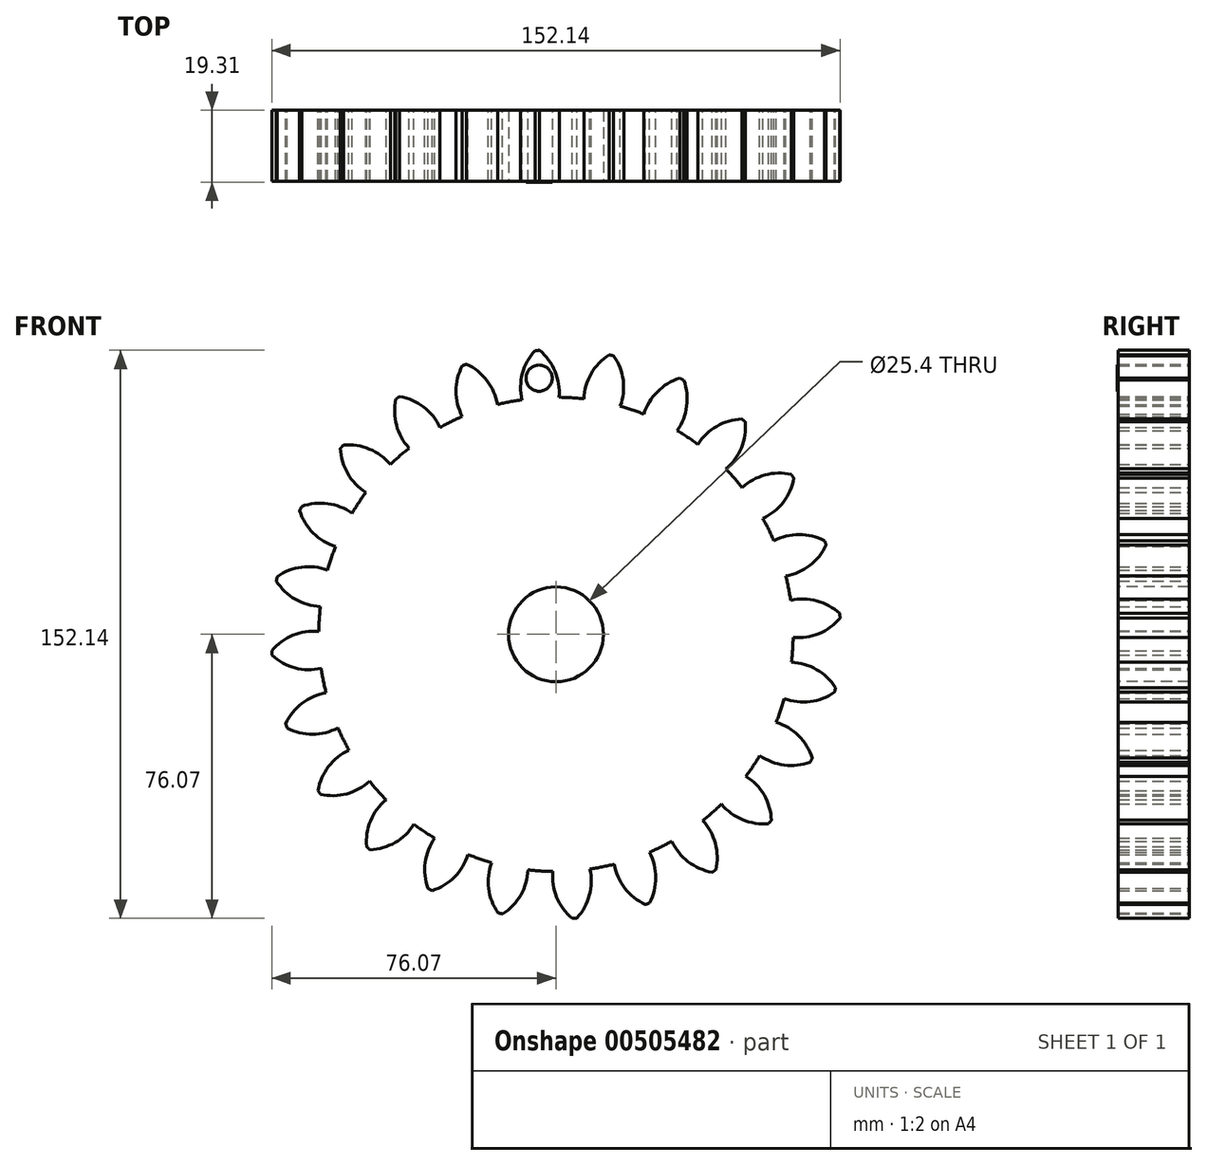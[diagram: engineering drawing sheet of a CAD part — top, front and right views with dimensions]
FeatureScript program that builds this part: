
annotation { "Feature Type Name" : "Feature", "Feature Type Description" : "" }
export const myFeature = defineFeature(function(context is Context, id is Id, definition is map)
    precondition{}
    {
        {
            var Q0;
            Q0=qCreatedBy(makeId("Front.planeOp"),FACE);
            var sketch = newSketch(context, id + "F0", { "sketchPlane" : qUnion([Q0])});
            skPoint(sketch, "E0.rect.middle", {"position": v(0, 0) * mm});
            skLineSegment(sketch, "E1", {"start": v(0, 0) * mm, "end": v(0, 76.2) * mm});
            skLineSegment(sketch, "E2", {"start": v(0, 0) * mm, "end": v(0, -76.2) * mm});
            skLineSegment(sketch, "E3", {"start": v(0, 0) * mm, "end": v(19.72, 73.6) * mm});
            skLineSegment(sketch, "E4", {"start": v(0, 0) * mm, "end": v(38.1, 66) * mm});
            skLineSegment(sketch, "E5", {"start": v(0, 0) * mm, "end": v(53.88, 53.88) * mm});
            skLineSegment(sketch, "E6", {"start": v(0, 0) * mm, "end": v(66, 38.1) * mm});
            skLineSegment(sketch, "E7", {"start": v(0, 0) * mm, "end": v(73.6, 19.72) * mm});
            skLineSegment(sketch, "E8", {"start": v(0, 0) * mm, "end": v(76.2, 0) * mm});
            skLineSegment(sketch, "E9", {"start": v(0, 0) * mm, "end": v(73.6, -19.72) * mm});
            skLineSegment(sketch, "E10", {"start": v(0, 0) * mm, "end": v(66, -38.1) * mm});
            skLineSegment(sketch, "E11", {"start": v(0, 0) * mm, "end": v(53.88, -53.88) * mm});
            skLineSegment(sketch, "E12", {"start": v(0, 0) * mm, "end": v(38.1, -66) * mm});
            skLineSegment(sketch, "E13", {"start": v(0, 0) * mm, "end": v(19.72, -73.6) * mm});
            skLineSegment(sketch, "E14", {"start": v(0, 0) * mm, "end": v(-19.72, -73.6) * mm});
            skLineSegment(sketch, "E15", {"start": v(0, 0) * mm, "end": v(-38.1, -66) * mm});
            skLineSegment(sketch, "E16", {"start": v(0, 0) * mm, "end": v(-53.88, -53.88) * mm});
            skLineSegment(sketch, "E17", {"start": v(0, 0) * mm, "end": v(-66, -38.1) * mm});
            skLineSegment(sketch, "E18", {"start": v(0, 0) * mm, "end": v(-73.6, -19.72) * mm});
            skLineSegment(sketch, "E19", {"start": v(0, 0) * mm, "end": v(-76.2, 0.07) * mm});
            skLineSegment(sketch, "E20", {"start": v(0, 0) * mm, "end": v(-73.6, 19.72) * mm});
            skLineSegment(sketch, "E21", {"start": v(0, 0) * mm, "end": v(-66, 38.1) * mm});
            skLineSegment(sketch, "E22", {"start": v(0, 0) * mm, "end": v(-53.88, 53.88) * mm});
            skLineSegment(sketch, "E23", {"start": v(0, 0) * mm, "end": v(-38.1, 66) * mm});
            skLineSegment(sketch, "E24", {"start": v(0, 0) * mm, "end": v(-19.72, 73.6) * mm});
            skCircle(sketch, "E25", {"center": v(0, 0) * mm, "radius": 76.2 * mm});
            skCircle(sketch, "E26", {"center": v(0, 0) * mm, "radius": 69.85 * mm});
            skCircle(sketch, "E27", {"center": v(0, 0) * mm, "radius": 63.5 * mm});
            skLineSegment(sketch, "E28", {"start": v(0, 0) * mm, "end": v(-4.98, 76.04) * mm});
            skLineSegment(sketch, "E29", {"start": v(0, 69.85) * mm, "end": v(-76.58, 69.85) * mm});
            skLineSegment(sketch, "E30", {"start": v(0, 69.85) * mm, "end": v(-76.5, 42) * mm});
            skLineSegment(sketch, "E31", {"start": v(-4.98, 76.04) * mm, "end": v(-7.15, 109.16) * mm});
            skLineSegment(sketch, "E32", {"start": v(0, 76.2) * mm, "end": v(0, 110.22) * mm});
            skCircle(sketch, "E33", {"center": v(0, 69.85) * mm, "radius": 14.6 * mm});
            skPoint(sketch, "E34", {"position": v(-13.72, 64.85) * mm});
            skArc(sketch, "E35", {"start": v(0.82, 63.5) * mm, "mid": v(-0.22, 70.43) * mm, "end": v(-4.37, 76.07) * mm});
            skArc(sketch, "E36.MirrorCS", {"start": v(-9.1, 62.84) * mm, "mid": v(-8.97, 69.85) * mm, "end": v(-5.6, 76) * mm});
            skSolve(sketch);
        }
        {
            var Q0;
            {var subQ1=sQuery(id+"F0.wireOp",EDGE,"E23");var subQ3=sQuery(id+"F0.wireOp",EDGE,"E27");var subQ4=makeQuery(id+"F0.imprint","INTERSECT",VERTEX,{"derivedFrom":[subQ1,subQ3]});Q0=makeQuery(id+"F0.imprint","IMPRINT",FACE,{"disambiguationData":[TD([[makeQuery(id+"F0.imprint","IMPRINT",EDGE,{"disambiguationData":[TD([[subQ4,1.0]])],"derivedFrom":subQ3}),1.0]])]});}
            var Q1;
            {var subQ1=sQuery(id+"F0.wireOp",EDGE,"E22");var subQ3=sQuery(id+"F0.wireOp",EDGE,"E27");var subQ4=makeQuery(id+"F0.imprint","INTERSECT",VERTEX,{"derivedFrom":[subQ1,subQ3]});Q1=makeQuery(id+"F0.imprint","IMPRINT",FACE,{"disambiguationData":[TD([[makeQuery(id+"F0.imprint","IMPRINT",EDGE,{"disambiguationData":[TD([[subQ4,1.0]])],"derivedFrom":subQ3}),1.0]])]});}
            var Q2;
            {var subQ1=sQuery(id+"F0.wireOp",EDGE,"E1");var subQ3=sQuery(id+"F0.wireOp",EDGE,"E33");var subQ4=makeQuery(id+"F0.imprint","INTERSECT",VERTEX,{"derivedFrom":[subQ1,subQ3]});Q2=makeQuery(id+"F0.imprint","IMPRINT",FACE,{"disambiguationData":[TD([[makeQuery(id+"F0.imprint","IMPRINT",EDGE,{"disambiguationData":[TD([[subQ4,1.0]])],"derivedFrom":subQ3}),-1.0]])]});}
            var Q3;
            {var subQ1=sQuery(id+"F0.wireOp",EDGE,"E19");var subQ3=sQuery(id+"F0.wireOp",EDGE,"E27");var subQ4=makeQuery(id+"F0.imprint","INTERSECT",VERTEX,{"derivedFrom":[subQ1,subQ3]});Q3=makeQuery(id+"F0.imprint","IMPRINT",FACE,{"disambiguationData":[TD([[makeQuery(id+"F0.imprint","IMPRINT",EDGE,{"disambiguationData":[TD([[subQ4,1.0]])],"derivedFrom":subQ3}),1.0]])]});}
            var Q4;
            {var subQ1=sQuery(id+"F0.wireOp",EDGE,"E24");var subQ3=sQuery(id+"F0.wireOp",EDGE,"E27");var subQ4=makeQuery(id+"F0.imprint","INTERSECT",VERTEX,{"derivedFrom":[subQ1,subQ3]});Q4=makeQuery(id+"F0.imprint","IMPRINT",FACE,{"disambiguationData":[TD([[makeQuery(id+"F0.imprint","IMPRINT",EDGE,{"disambiguationData":[TD([[subQ4,1.0]])],"derivedFrom":subQ3}),1.0]])]});}
            var Q5;
            {var subQ1=sQuery(id+"F0.wireOp",EDGE,"E20");var subQ3=sQuery(id+"F0.wireOp",EDGE,"E27");var subQ4=makeQuery(id+"F0.imprint","INTERSECT",VERTEX,{"derivedFrom":[subQ1,subQ3]});Q5=makeQuery(id+"F0.imprint","IMPRINT",FACE,{"disambiguationData":[TD([[makeQuery(id+"F0.imprint","IMPRINT",EDGE,{"disambiguationData":[TD([[subQ4,1.0]])],"derivedFrom":subQ3}),1.0]])]});}
            var Q6;
            {var subQ1=sQuery(id+"F0.wireOp",EDGE,"E21");var subQ3=sQuery(id+"F0.wireOp",EDGE,"E27");var subQ4=makeQuery(id+"F0.imprint","INTERSECT",VERTEX,{"derivedFrom":[subQ1,subQ3]});Q6=makeQuery(id+"F0.imprint","IMPRINT",FACE,{"disambiguationData":[TD([[makeQuery(id+"F0.imprint","IMPRINT",EDGE,{"disambiguationData":[TD([[subQ4,1.0]])],"derivedFrom":subQ3}),1.0]])]});}
            var Q7;
            {var subQ1=sQuery(id+"F0.wireOp",EDGE,"E6");var subQ3=sQuery(id+"F0.wireOp",EDGE,"E27");var subQ4=makeQuery(id+"F0.imprint","INTERSECT",VERTEX,{"derivedFrom":[subQ1,subQ3]});Q7=makeQuery(id+"F0.imprint","IMPRINT",FACE,{"disambiguationData":[TD([[makeQuery(id+"F0.imprint","IMPRINT",EDGE,{"disambiguationData":[TD([[subQ4,1.0]])],"derivedFrom":subQ3}),1.0]])]});}
            var Q8;
            {var subQ1=sQuery(id+"F0.wireOp",EDGE,"E4");var subQ3=sQuery(id+"F0.wireOp",EDGE,"E27");var subQ4=makeQuery(id+"F0.imprint","INTERSECT",VERTEX,{"derivedFrom":[subQ1,subQ3]});Q8=makeQuery(id+"F0.imprint","IMPRINT",FACE,{"disambiguationData":[TD([[makeQuery(id+"F0.imprint","IMPRINT",EDGE,{"disambiguationData":[TD([[subQ4,1.0]])],"derivedFrom":subQ3}),1.0]])]});}
            var Q9;
            {var subQ1=sQuery(id+"F0.wireOp",EDGE,"E7");var subQ3=sQuery(id+"F0.wireOp",EDGE,"E27");var subQ4=makeQuery(id+"F0.imprint","INTERSECT",VERTEX,{"derivedFrom":[subQ1,subQ3]});Q9=makeQuery(id+"F0.imprint","IMPRINT",FACE,{"disambiguationData":[TD([[makeQuery(id+"F0.imprint","IMPRINT",EDGE,{"disambiguationData":[TD([[subQ4,1.0]])],"derivedFrom":subQ3}),1.0]])]});}
            var Q10;
            {var subQ0=sQuery(id+"F0.wireOp",EDGE,"E3");var subQ5=sQuery(id+"F0.wireOp",EDGE,"E27");var subQ6=makeQuery(id+"F0.imprint","INTERSECT",VERTEX,{"derivedFrom":[subQ0,subQ5]});Q10=makeQuery(id+"F0.imprint","IMPRINT",FACE,{"disambiguationData":[TD([[makeQuery(id+"F0.imprint","IMPRINT",EDGE,{"disambiguationData":[TD([[subQ6,-1.0]])],"derivedFrom":subQ5}),1.0]])]});}
            var Q11;
            {var subQ1=sQuery(id+"F0.wireOp",EDGE,"E3");var subQ3=sQuery(id+"F0.wireOp",EDGE,"E27");var subQ4=makeQuery(id+"F0.imprint","INTERSECT",VERTEX,{"derivedFrom":[subQ1,subQ3]});Q11=makeQuery(id+"F0.imprint","IMPRINT",FACE,{"disambiguationData":[TD([[makeQuery(id+"F0.imprint","IMPRINT",EDGE,{"disambiguationData":[TD([[subQ4,1.0]])],"derivedFrom":subQ3}),1.0]])]});}
            var Q12;
            {var subQ1=sQuery(id+"F0.wireOp",EDGE,"E5");var subQ3=sQuery(id+"F0.wireOp",EDGE,"E27");var subQ4=makeQuery(id+"F0.imprint","INTERSECT",VERTEX,{"derivedFrom":[subQ1,subQ3]});Q12=makeQuery(id+"F0.imprint","IMPRINT",FACE,{"disambiguationData":[TD([[makeQuery(id+"F0.imprint","IMPRINT",EDGE,{"disambiguationData":[TD([[subQ4,1.0]])],"derivedFrom":subQ3}),1.0]])]});}
            var Q13;
            {var subQ1=sQuery(id+"F0.wireOp",EDGE,"E17");var subQ3=sQuery(id+"F0.wireOp",EDGE,"E27");var subQ4=makeQuery(id+"F0.imprint","INTERSECT",VERTEX,{"derivedFrom":[subQ1,subQ3]});Q13=makeQuery(id+"F0.imprint","IMPRINT",FACE,{"disambiguationData":[TD([[makeQuery(id+"F0.imprint","IMPRINT",EDGE,{"disambiguationData":[TD([[subQ4,1.0]])],"derivedFrom":subQ3}),1.0]])]});}
            var Q14;
            {var subQ1=sQuery(id+"F0.wireOp",EDGE,"E15");var subQ3=sQuery(id+"F0.wireOp",EDGE,"E27");var subQ4=makeQuery(id+"F0.imprint","INTERSECT",VERTEX,{"derivedFrom":[subQ1,subQ3]});Q14=makeQuery(id+"F0.imprint","IMPRINT",FACE,{"disambiguationData":[TD([[makeQuery(id+"F0.imprint","IMPRINT",EDGE,{"disambiguationData":[TD([[subQ4,1.0]])],"derivedFrom":subQ3}),1.0]])]});}
            var Q15;
            {var subQ1=sQuery(id+"F0.wireOp",EDGE,"E16");var subQ3=sQuery(id+"F0.wireOp",EDGE,"E27");var subQ4=makeQuery(id+"F0.imprint","INTERSECT",VERTEX,{"derivedFrom":[subQ1,subQ3]});Q15=makeQuery(id+"F0.imprint","IMPRINT",FACE,{"disambiguationData":[TD([[makeQuery(id+"F0.imprint","IMPRINT",EDGE,{"disambiguationData":[TD([[subQ4,1.0]])],"derivedFrom":subQ3}),1.0]])]});}
            var Q16;
            {var subQ1=sQuery(id+"F0.wireOp",EDGE,"E2");var subQ3=sQuery(id+"F0.wireOp",EDGE,"E27");var subQ4=makeQuery(id+"F0.imprint","INTERSECT",VERTEX,{"derivedFrom":[subQ1,subQ3]});Q16=makeQuery(id+"F0.imprint","IMPRINT",FACE,{"disambiguationData":[TD([[makeQuery(id+"F0.imprint","IMPRINT",EDGE,{"disambiguationData":[TD([[subQ4,1.0]])],"derivedFrom":subQ3}),1.0]])]});}
            var Q17;
            {var subQ1=sQuery(id+"F0.wireOp",EDGE,"E14");var subQ3=sQuery(id+"F0.wireOp",EDGE,"E27");var subQ4=makeQuery(id+"F0.imprint","INTERSECT",VERTEX,{"derivedFrom":[subQ1,subQ3]});Q17=makeQuery(id+"F0.imprint","IMPRINT",FACE,{"disambiguationData":[TD([[makeQuery(id+"F0.imprint","IMPRINT",EDGE,{"disambiguationData":[TD([[subQ4,1.0]])],"derivedFrom":subQ3}),1.0]])]});}
            var Q18;
            {var subQ1=sQuery(id+"F0.wireOp",EDGE,"E18");var subQ3=sQuery(id+"F0.wireOp",EDGE,"E27");var subQ4=makeQuery(id+"F0.imprint","INTERSECT",VERTEX,{"derivedFrom":[subQ1,subQ3]});Q18=makeQuery(id+"F0.imprint","IMPRINT",FACE,{"disambiguationData":[TD([[makeQuery(id+"F0.imprint","IMPRINT",EDGE,{"disambiguationData":[TD([[subQ4,1.0]])],"derivedFrom":subQ3}),1.0]])]});}
            var Q19;
            {var subQ0=sQuery(id+"F0.wireOp",EDGE,"E33");var subQ1=sQuery(id+"F0.wireOp",EDGE,"E1");var subQ2=makeQuery(id+"F0.imprint","INTERSECT",VERTEX,{"derivedFrom":[subQ1,subQ0]});Q19=makeQuery(id+"F0.imprint","IMPRINT",FACE,{"disambiguationData":[TD([[makeQuery(id+"F0.imprint","IMPRINT",EDGE,{"disambiguationData":[TD([[subQ2,-1.0]])],"derivedFrom":subQ1}),1.0]])]});}
            var Q20;
            {var subQ0=sQuery(id+"F0.wireOp",EDGE,"E27");var subQ1=makeQuery(id+"F0.imprint","INTERSECT",VERTEX,{"derivedFrom":[subQ0,sQuery(id+"F0.wireOp",EDGE,"E36.MirrorCS")]});Q20=makeQuery(id+"F0.imprint","IMPRINT",FACE,{"disambiguationData":[TD([[makeQuery(id+"F0.imprint","IMPRINT",EDGE,{"disambiguationData":[TD([[subQ1,1.0]])],"derivedFrom":subQ0}),1.0]])]});}
            var Q21;
            {var subQ0=sQuery(id+"F0.wireOp",EDGE,"E33");var subQ1=sQuery(id+"F0.wireOp",EDGE,"E1");var subQ2=makeQuery(id+"F0.imprint","INTERSECT",VERTEX,{"derivedFrom":[subQ1,subQ0]});Q21=makeQuery(id+"F0.imprint","IMPRINT",FACE,{"disambiguationData":[TD([[makeQuery(id+"F0.imprint","IMPRINT",EDGE,{"disambiguationData":[TD([[subQ2,-1.0]])],"derivedFrom":subQ1}),-1.0]])]});}
            var Q22;
            {var subQ1=sQuery(id+"F0.wireOp",EDGE,"E1");var subQ3=sQuery(id+"F0.wireOp",EDGE,"E27");var subQ4=makeQuery(id+"F0.imprint","INTERSECT",VERTEX,{"derivedFrom":[subQ1,subQ3]});Q22=makeQuery(id+"F0.imprint","IMPRINT",FACE,{"disambiguationData":[TD([[makeQuery(id+"F0.imprint","IMPRINT",EDGE,{"disambiguationData":[TD([[subQ4,-1.0]])],"derivedFrom":subQ3}),-1.0]])]});}
            var Q23;
            {var subQ0=sQuery(id+"F0.wireOp",EDGE,"E36.MirrorCS");var subQ1=sQuery(id+"F0.wireOp",EDGE,"E27");var subQ2=makeQuery(id+"F0.imprint","INTERSECT",VERTEX,{"derivedFrom":[subQ1,subQ0]});Q23=makeQuery(id+"F0.imprint","IMPRINT",FACE,{"disambiguationData":[TD([[makeQuery(id+"F0.imprint","IMPRINT",EDGE,{"disambiguationData":[TD([[subQ2,1.0]])],"derivedFrom":subQ1}),-1.0]])]});}
            var Q24;
            {var subQ0=sQuery(id+"F0.wireOp",EDGE,"E28");var subQ1=sQuery(id+"F0.wireOp",EDGE,"E26");var subQ2=makeQuery(id+"F0.imprint","INTERSECT",VERTEX,{"derivedFrom":[subQ1,subQ0]});Q24=makeQuery(id+"F0.imprint","IMPRINT",FACE,{"disambiguationData":[TD([[makeQuery(id+"F0.imprint","IMPRINT",EDGE,{"disambiguationData":[TD([[subQ2,-1.0]])],"derivedFrom":subQ1}),1.0]])]});}
            var Q25;
            {var subQ0=sQuery(id+"F0.wireOp",EDGE,"E28");var subQ1=sQuery(id+"F0.wireOp",EDGE,"E26");var subQ2=makeQuery(id+"F0.imprint","INTERSECT",VERTEX,{"derivedFrom":[subQ1,subQ0]});Q25=makeQuery(id+"F0.imprint","IMPRINT",FACE,{"disambiguationData":[TD([[makeQuery(id+"F0.imprint","IMPRINT",EDGE,{"disambiguationData":[TD([[subQ2,-1.0]])],"derivedFrom":subQ1}),-1.0]])]});}
            var Q26;
            {var subQ0=sQuery(id+"F0.wireOp",EDGE,"E28");var subQ5=sQuery(id+"F0.wireOp",EDGE,"E29");var subQ6=makeQuery(id+"F0.imprint","INTERSECT",VERTEX,{"derivedFrom":[subQ0,subQ5]});Q26=makeQuery(id+"F0.imprint","IMPRINT",FACE,{"disambiguationData":[TD([[makeQuery(id+"F0.imprint","IMPRINT",EDGE,{"disambiguationData":[TD([[subQ6,-1.0]])],"derivedFrom":subQ5}),-1.0]])]});}
            var Q27;
            {var subQ1=sQuery(id+"F0.wireOp",EDGE,"E25");var subQ3=sQuery(id+"F0.wireOp",EDGE,"E35");var subQ4=makeQuery(id+"F0.imprint","INTERSECT",VERTEX,{"derivedFrom":[subQ1,subQ3]});Q27=makeQuery(id+"F0.imprint","IMPRINT",FACE,{"disambiguationData":[TD([[makeQuery(id+"F0.imprint","IMPRINT",EDGE,{"disambiguationData":[TD([[subQ4,-1.0]])],"derivedFrom":subQ1}),1.0]])]});}
            var Q28;
            {var subQ0=sQuery(id+"F0.wireOp",EDGE,"E35");var subQ3=sQuery(id+"F0.wireOp",EDGE,"E27");var subQ5=makeQuery(id+"F0.imprint","INTERSECT",VERTEX,{"derivedFrom":[subQ3,subQ0]});Q28=makeQuery(id+"F0.imprint","IMPRINT",FACE,{"disambiguationData":[TD([[makeQuery(id+"F0.imprint","IMPRINT",EDGE,{"disambiguationData":[TD([[subQ5,-1.0]])],"derivedFrom":subQ3}),-1.0]])]});}
            var Q29;
            {var subQ1=sQuery(id+"F0.wireOp",EDGE,"E26");var subQ3=sQuery(id+"F0.wireOp",EDGE,"E28");var subQ4=makeQuery(id+"F0.imprint","INTERSECT",VERTEX,{"derivedFrom":[subQ1,subQ3]});Q29=makeQuery(id+"F0.imprint","IMPRINT",FACE,{"disambiguationData":[TD([[makeQuery(id+"F0.imprint","IMPRINT",EDGE,{"disambiguationData":[TD([[subQ4,-1.0]])],"derivedFrom":subQ3}),-1.0]])]});}
            var Q30;
            {var subQ1=sQuery(id+"F0.wireOp",EDGE,"E26");var subQ3=sQuery(id+"F0.wireOp",EDGE,"E28");var subQ4=makeQuery(id+"F0.imprint","INTERSECT",VERTEX,{"derivedFrom":[subQ1,subQ3]});Q30=makeQuery(id+"F0.imprint","IMPRINT",FACE,{"disambiguationData":[TD([[makeQuery(id+"F0.imprint","IMPRINT",EDGE,{"disambiguationData":[TD([[subQ4,1.0]])],"derivedFrom":subQ3}),-1.0]])]});}
            var Q31;
            {var subQ1=sQuery(id+"F0.wireOp",EDGE,"E10");var subQ3=sQuery(id+"F0.wireOp",EDGE,"E27");var subQ4=makeQuery(id+"F0.imprint","INTERSECT",VERTEX,{"derivedFrom":[subQ1,subQ3]});Q31=makeQuery(id+"F0.imprint","IMPRINT",FACE,{"disambiguationData":[TD([[makeQuery(id+"F0.imprint","IMPRINT",EDGE,{"disambiguationData":[TD([[subQ4,1.0]])],"derivedFrom":subQ3}),1.0]])]});}
            var Q32;
            {var subQ1=sQuery(id+"F0.wireOp",EDGE,"E9");var subQ3=sQuery(id+"F0.wireOp",EDGE,"E27");var subQ4=makeQuery(id+"F0.imprint","INTERSECT",VERTEX,{"derivedFrom":[subQ1,subQ3]});Q32=makeQuery(id+"F0.imprint","IMPRINT",FACE,{"disambiguationData":[TD([[makeQuery(id+"F0.imprint","IMPRINT",EDGE,{"disambiguationData":[TD([[subQ4,1.0]])],"derivedFrom":subQ3}),1.0]])]});}
            var Q33;
            {var subQ1=sQuery(id+"F0.wireOp",EDGE,"E8");var subQ3=sQuery(id+"F0.wireOp",EDGE,"E27");var subQ4=makeQuery(id+"F0.imprint","INTERSECT",VERTEX,{"derivedFrom":[subQ1,subQ3]});Q33=makeQuery(id+"F0.imprint","IMPRINT",FACE,{"disambiguationData":[TD([[makeQuery(id+"F0.imprint","IMPRINT",EDGE,{"disambiguationData":[TD([[subQ4,1.0]])],"derivedFrom":subQ3}),1.0]])]});}
            var Q34;
            {var subQ1=sQuery(id+"F0.wireOp",EDGE,"E11");var subQ3=sQuery(id+"F0.wireOp",EDGE,"E27");var subQ4=makeQuery(id+"F0.imprint","INTERSECT",VERTEX,{"derivedFrom":[subQ1,subQ3]});Q34=makeQuery(id+"F0.imprint","IMPRINT",FACE,{"disambiguationData":[TD([[makeQuery(id+"F0.imprint","IMPRINT",EDGE,{"disambiguationData":[TD([[subQ4,1.0]])],"derivedFrom":subQ3}),1.0]])]});}
            var Q35;
            {var subQ1=sQuery(id+"F0.wireOp",EDGE,"E2");var subQ3=sQuery(id+"F0.wireOp",EDGE,"E27");var subQ4=makeQuery(id+"F0.imprint","INTERSECT",VERTEX,{"derivedFrom":[subQ1,subQ3]});Q35=makeQuery(id+"F0.imprint","IMPRINT",FACE,{"disambiguationData":[TD([[makeQuery(id+"F0.imprint","IMPRINT",EDGE,{"disambiguationData":[TD([[subQ4,-1.0]])],"derivedFrom":subQ3}),1.0]])]});}
            var Q36;
            {var subQ1=sQuery(id+"F0.wireOp",EDGE,"E12");var subQ3=sQuery(id+"F0.wireOp",EDGE,"E27");var subQ4=makeQuery(id+"F0.imprint","INTERSECT",VERTEX,{"derivedFrom":[subQ1,subQ3]});Q36=makeQuery(id+"F0.imprint","IMPRINT",FACE,{"disambiguationData":[TD([[makeQuery(id+"F0.imprint","IMPRINT",EDGE,{"disambiguationData":[TD([[subQ4,1.0]])],"derivedFrom":subQ3}),1.0]])]});}
            extrude(context, id + "F1", {"entities" : qUnion([Q0, Q1, Q2, Q3, Q4, Q5, Q6, Q7, Q8, Q9, Q10, Q11, Q12, Q13, Q14, Q15, Q16, Q17, Q18, Q19, Q20, Q21, Q22, Q23, Q24, Q25, Q26, Q27, Q28, Q29, Q30, Q31, Q32, Q33, Q34, Q35, Q36]), "endBound" : BoundingType.SYMMETRIC, "depth" : 19.05 * mm});
        }
        {
            var Q0;
            Q0=makeQuery(id+"F1.opExtrude","SWEPT_BODY",BODY,{"disambiguationData":[OSD([sQuery(id+"F0.wireOp",EDGE,"E25"),sQuery(id+"F0.wireOp",EDGE,"E27"),sQuery(id+"F0.wireOp",EDGE,"E35"),sQuery(id+"F0.wireOp",EDGE,"E36.MirrorCS")])]});
            var Q1;
            Q1=makeQuery(id+"F1.opExtrude","SWEPT_FACE",FACE,{"disambiguationData":[OSD([sQuery(id+"F0.wireOp",EDGE,"E27")])]});
            circularPattern(context, id + "F2", {"operationType" : NewBodyOperationType.ADD, "entities" : qUnion([Q0]), "axis" : qUnion([Q1]), "angle" : 15 * degree, "instanceCount" : 24});
        }
        {
            var Q0;
            Q0=makeQuery(id+"F1.opExtrude","CAP_FACE",FACE,{"disambiguationData":[OSD([sQuery(id+"F0.wireOp",EDGE,"E25"),sQuery(id+"F0.wireOp",EDGE,"E27"),sQuery(id+"F0.wireOp",EDGE,"E35"),sQuery(id+"F0.wireOp",EDGE,"E36.MirrorCS")])],"isStart":false});
            var sketch = newSketch(context, id + "F3", { "sketchPlane" : qUnion([Q0])});
            skPoint(sketch, "E37", {"position": v(0, 0) * mm});
            skSolve(sketch);
        }
        {
            var Q0;
            Q0=sQuery(id+"F3.wireOp",VERTEX,"E37");
            var Q1;
            Q1=makeQuery(id+"F1.opExtrude","SWEPT_BODY",BODY,{"disambiguationData":[OSD([sQuery(id+"F0.wireOp",EDGE,"E25"),sQuery(id+"F0.wireOp",EDGE,"E27"),sQuery(id+"F0.wireOp",EDGE,"E35"),sQuery(id+"F0.wireOp",EDGE,"E36.MirrorCS")])]});
            hole(context, id + "F4", {"style" : HoleStyle.SIMPLE, "holeDiameter" : 25.4 * mm, "endStyle" : HoleEndStyle.THROUGH, "locations" : qUnion([Q0]), "scope" : qUnion([Q1]), "tappedDepth" : 12.7 * mm, "tapClearance" : 3});
        }
        {
            var Q0;
            {var subQ0=makeQuery(id+"F1.opExtrude","CAP_FACE",FACE,{"disambiguationData":[OSD([sQuery(id+"F0.wireOp",EDGE,"E25"),sQuery(id+"F0.wireOp",EDGE,"E27"),sQuery(id+"F0.wireOp",EDGE,"E35"),sQuery(id+"F0.wireOp",EDGE,"E36.MirrorCS")])],"isStart":false});Q0=makeQuery(id+"F2.boolean.opBoolean","MERGE",FACE,{"derivedFrom":[subQ0,makeQuery(id+"F2.opPattern","COPY",FACE,{"derivedFrom":subQ0,"instanceName":"1"}),makeQuery(id+"F2.opPattern","COPY",FACE,{"derivedFrom":subQ0,"instanceName":"2"}),makeQuery(id+"F2.opPattern","COPY",FACE,{"derivedFrom":subQ0,"instanceName":"3"}),makeQuery(id+"F2.opPattern","COPY",FACE,{"derivedFrom":subQ0,"instanceName":"4"}),makeQuery(id+"F2.opPattern","COPY",FACE,{"derivedFrom":subQ0,"instanceName":"5"}),makeQuery(id+"F2.opPattern","COPY",FACE,{"derivedFrom":subQ0,"instanceName":"6"}),makeQuery(id+"F2.opPattern","COPY",FACE,{"derivedFrom":subQ0,"instanceName":"7"}),makeQuery(id+"F2.opPattern","COPY",FACE,{"derivedFrom":subQ0,"instanceName":"8"}),makeQuery(id+"F2.opPattern","COPY",FACE,{"derivedFrom":subQ0,"instanceName":"9"}),makeQuery(id+"F2.opPattern","COPY",FACE,{"derivedFrom":subQ0,"instanceName":"10"}),makeQuery(id+"F2.opPattern","COPY",FACE,{"derivedFrom":subQ0,"instanceName":"11"}),makeQuery(id+"F2.opPattern","COPY",FACE,{"derivedFrom":subQ0,"instanceName":"12"}),makeQuery(id+"F2.opPattern","COPY",FACE,{"derivedFrom":subQ0,"instanceName":"13"}),makeQuery(id+"F2.opPattern","COPY",FACE,{"derivedFrom":subQ0,"instanceName":"14"}),makeQuery(id+"F2.opPattern","COPY",FACE,{"derivedFrom":subQ0,"instanceName":"15"}),makeQuery(id+"F2.opPattern","COPY",FACE,{"derivedFrom":subQ0,"instanceName":"16"}),makeQuery(id+"F2.opPattern","COPY",FACE,{"derivedFrom":subQ0,"instanceName":"17"}),makeQuery(id+"F2.opPattern","COPY",FACE,{"derivedFrom":subQ0,"instanceName":"18"}),makeQuery(id+"F2.opPattern","COPY",FACE,{"derivedFrom":subQ0,"instanceName":"19"}),makeQuery(id+"F2.opPattern","COPY",FACE,{"derivedFrom":subQ0,"instanceName":"20"}),makeQuery(id+"F2.opPattern","COPY",FACE,{"derivedFrom":subQ0,"instanceName":"21"}),makeQuery(id+"F2.opPattern","COPY",FACE,{"derivedFrom":subQ0,"instanceName":"22"}),makeQuery(id+"F2.opPattern","COPY",FACE,{"derivedFrom":subQ0,"instanceName":"23"})]});}
            var sketch = newSketch(context, id + "F5", { "sketchPlane" : qUnion([Q0])});
            skCircle(sketch, "E38", {"center": v(-4.51, 68.62) * mm, "radius": 3.51 * mm});
            skSolve(sketch);
        }
        {
            var Q0;
            Q0=makeQuery(id+"F5.imprint","IMPRINT",FACE,{"disambiguationData":[TD([[makeQuery(id+"F5.imprint","IMPRINT",EDGE,{"derivedFrom":sQuery(id+"F5.wireOp",EDGE,"E38")}),1.0]])]});
            extrude(context, id + "F6", {"entities" : qUnion([Q0]), "operationType" : NewBodyOperationType.ADD, "depth" : 0.25 * mm});
        }
    });
